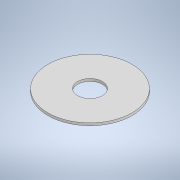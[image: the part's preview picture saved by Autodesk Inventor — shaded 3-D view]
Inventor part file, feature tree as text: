
AUTODESK INVENTOR PART (.ipt)
format: ipt  version: 2021 (Build 250183000, 183)  size: 95,744 bytes
history: native  units: mm
features: extrude x1, sketch x1
ambient origin geometry x8: Origin, YZ Plane, XZ Plane, XY Plane, X Axis, Y Axis, Z Axis, Center Point
bodies: Solid1 (feature_tree)
feature tree (2):
  extrude  "Extrusion1"  Depth=0.5mm
  sketch  "Sketch1"  dims[d0=17.0mm d1=5.0mm d2=0.5mm d3=0.0mm]
